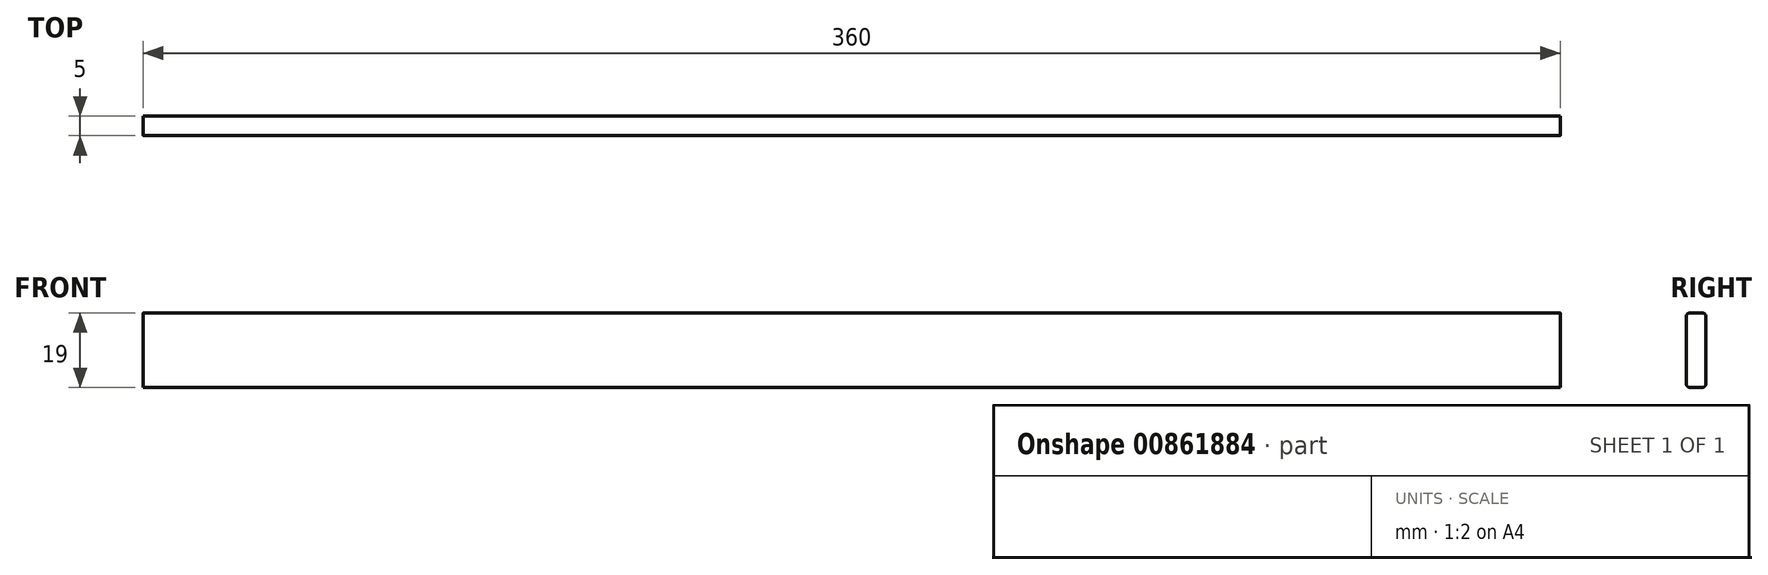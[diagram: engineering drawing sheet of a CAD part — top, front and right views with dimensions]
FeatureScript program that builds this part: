
annotation { "Feature Type Name" : "Feature", "Feature Type Description" : "" }
export const myFeature = defineFeature(function(context is Context, id is Id, definition is map)
    precondition{}
    {
        {
            var Q0;
            Q0=qCreatedBy(makeId("Front.planeOp"),FACE);
            var sketch = newSketch(context, id + "F0", { "sketchPlane" : qUnion([Q0])});
            skLineSegment(sketch, "E0.bottom", {"start": v(-180, 9.5) * mm, "end": v(180, 9.5) * mm});
            skLineSegment(sketch, "E0.top", {"start": v(-180, -9.5) * mm, "end": v(180, -9.5) * mm});
            skLineSegment(sketch, "E0.left", {"start": v(-180, 9.5) * mm, "end": v(-180, -9.5) * mm});
            skLineSegment(sketch, "E0.right", {"start": v(180, 9.5) * mm, "end": v(180, -9.5) * mm});
            skPoint(sketch, "E0.middle", {"position": v(0, 0) * mm});
            skSolve(sketch);
        }
        {
            var Q0;
            Q0=makeQuery(id+"F0.imprint","IMPRINT",FACE,{"disambiguationData":[TD([[makeQuery(id+"F0.imprint","IMPRINT",EDGE,{"derivedFrom":sQuery(id+"F0.wireOp",EDGE,"E0.bottom")}),-1.0]])]});
            extrude(context, id + "F1", {"entities" : qUnion([Q0]), "depth" : 5 * mm, "offsetDistance" : 25 * mm});
        }
        {
            var Q0;
            Q0=makeQuery(id+"F1.opExtrude","CAP_EDGE",EDGE,{"disambiguationData":[OSD([sQuery(id+"F0.wireOp",EDGE,"E0.bottom")])],"isStart":false});
            var Q1;
            Q1=makeQuery(id+"F1.opExtrude","CAP_EDGE",EDGE,{"disambiguationData":[OSD([sQuery(id+"F0.wireOp",EDGE,"E0.bottom")])],"isStart":true});
            var Q2;
            Q2=makeQuery(id+"F1.opExtrude","CAP_EDGE",EDGE,{"disambiguationData":[OSD([sQuery(id+"F0.wireOp",EDGE,"E0.top")])],"isStart":false});
            var Q3;
            Q3=makeQuery(id+"F1.opExtrude","CAP_EDGE",EDGE,{"disambiguationData":[OSD([sQuery(id+"F0.wireOp",EDGE,"E0.top")])],"isStart":true});
            fillet(context, id + "F2", {"entities" : qUnion([Q0, Q1, Q2, Q3]), "radius" : 1 * mm, "tangentPropagation" : true, "allowEdgeOverflow" : false});
        }
    });
